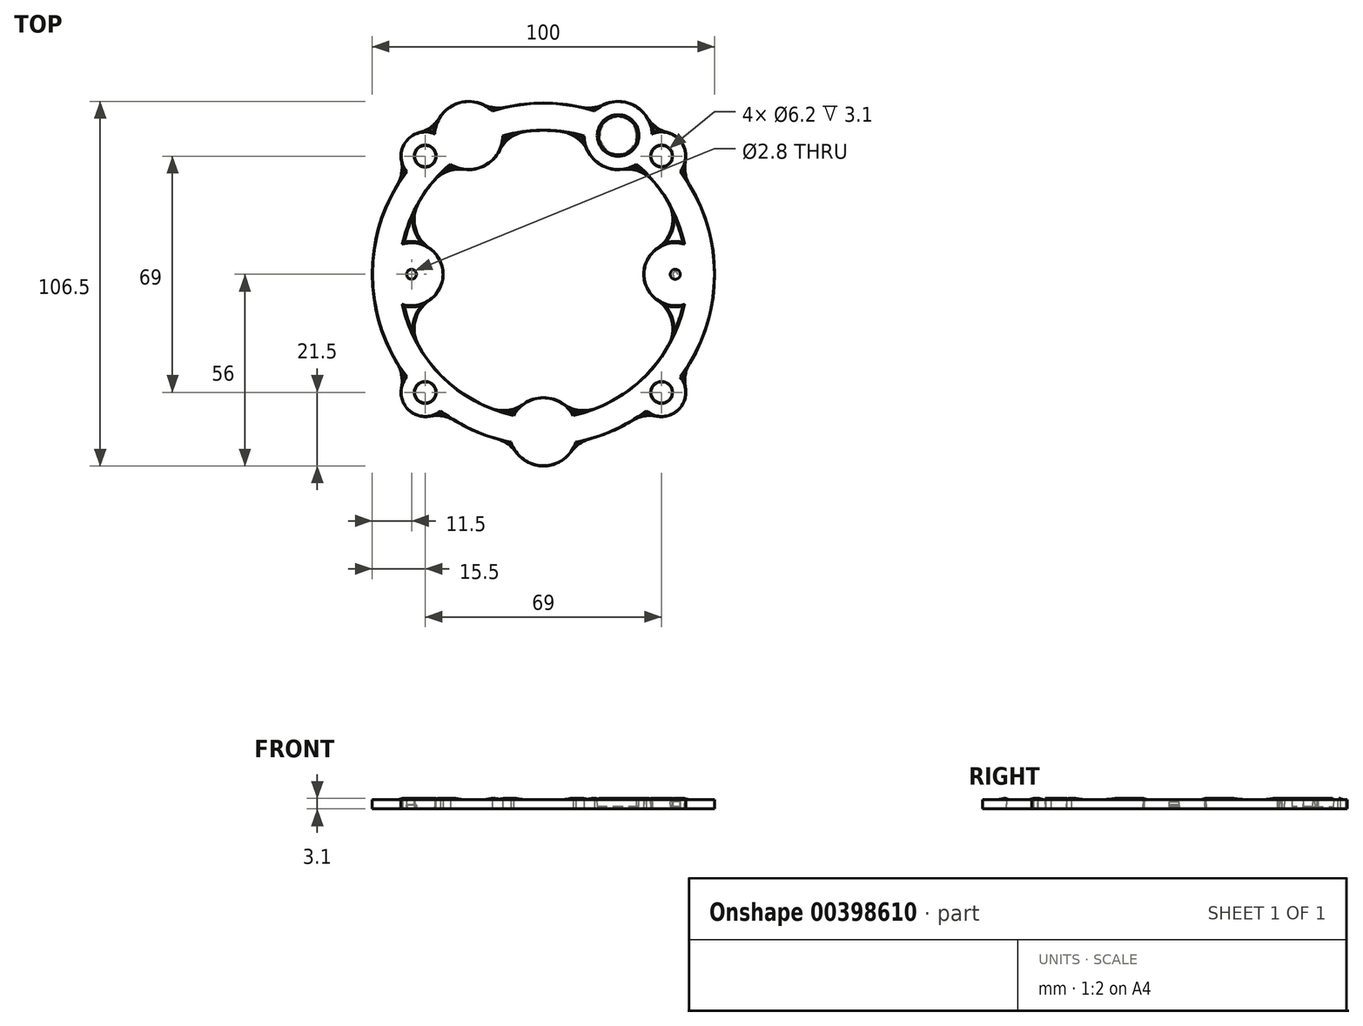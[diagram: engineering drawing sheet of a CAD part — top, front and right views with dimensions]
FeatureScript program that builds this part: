
annotation { "Feature Type Name" : "Feature", "Feature Type Description" : "" }
export const myFeature = defineFeature(function(context is Context, id is Id, definition is map)
    precondition{}
    {
        {
            var Q0;
            Q0=qCreatedBy(makeId("Top.planeOp"),FACE);
            var sketch = newSketch(context, id + "F0", { "sketchPlane" : qUnion([Q0])});
            skCircle(sketch, "E0", {"center": v(0, 0) * mm, "radius": 56 * mm, "construction": true});
            skCircle(sketch, "E1", {"center": v(0, 0) * mm, "radius": 38.5 * mm, "construction": true});
            skLineSegment(sketch, "E2.bottom", {"start": v(-34.5, 34.5) * mm, "end": v(34.5, 34.5) * mm, "construction": true});
            skLineSegment(sketch, "E2.top", {"start": v(-34.5, -34.5) * mm, "end": v(34.5, -34.5) * mm, "construction": true});
            skLineSegment(sketch, "E2.left", {"start": v(-34.5, 34.5) * mm, "end": v(-34.5, -34.5) * mm, "construction": true});
            skLineSegment(sketch, "E2.right", {"start": v(34.5, 34.5) * mm, "end": v(34.5, -34.5) * mm, "construction": true});
            skCircle(sketch, "E3", {"center": v(-34.5, 34.5) * mm, "radius": 3.1 * mm});
            skCircle(sketch, "E4.1.0", {"center": v(-34.5, -34.5) * mm, "radius": 3.1 * mm});
            skCircle(sketch, "E4.2.0", {"center": v(34.5, -34.5) * mm, "radius": 3.1 * mm});
            skCircle(sketch, "E4.3.0", {"center": v(34.5, 34.5) * mm, "radius": 3.1 * mm});
            skCircle(sketch, "E5", {"center": v(-38.5, 0) * mm, "radius": 1.4 * mm});
            skPoint(sketch, "E5.centerSnap0", {"position": v(-34.5, 0) * mm});
            skCircle(sketch, "E6.MirrorC", {"center": v(38.5, 0) * mm, "radius": 1.4 * mm});
            skCircle(sketch, "E7", {"center": v(-21.81, 40.5) * mm, "radius": 6 * mm});
            skCircle(sketch, "E8.MirrorC", {"center": v(21.81, 40.5) * mm, "radius": 6 * mm});
            skLineSegment(sketch, "E9.bottom", {"start": v(-24.25, 29.25) * mm, "end": v(24.25, 29.25) * mm});
            skLineSegment(sketch, "E9.top", {"start": v(-24.25, -29.25) * mm, "end": v(24.25, -29.25) * mm});
            skLineSegment(sketch, "E9.left", {"start": v(-29.25, 24.25) * mm, "end": v(-29.25, -24.25) * mm});
            skLineSegment(sketch, "E9.right", {"start": v(29.25, 24.25) * mm, "end": v(29.25, -24.25) * mm});
            skPoint(sketch, "E10.visualSharp", {"position": v(-29.25, 29.25) * mm});
            skArc(sketch, "E10.filletArc", {"start": v(-24.25, 29.25) * mm, "mid": v(-27.79, 27.79) * mm, "end": v(-29.25, 24.25) * mm});
            skPoint(sketch, "E11.visualSharp", {"position": v(29.25, 29.25) * mm});
            skArc(sketch, "E11.filletArc", {"start": v(29.25, 24.25) * mm, "mid": v(27.79, 27.79) * mm, "end": v(24.25, 29.25) * mm});
            skPoint(sketch, "E12.visualSharp", {"position": v(29.25, -29.25) * mm});
            skArc(sketch, "E12.filletArc", {"start": v(24.25, -29.25) * mm, "mid": v(27.79, -27.79) * mm, "end": v(29.25, -24.25) * mm});
            skPoint(sketch, "E13.visualSharp", {"position": v(-29.25, -29.25) * mm});
            skArc(sketch, "E13.filletArc", {"start": v(-29.25, -24.25) * mm, "mid": v(-27.79, -27.79) * mm, "end": v(-24.25, -29.25) * mm});
            skCircle(sketch, "E14", {"center": v(0, -46) * mm, "radius": 6 * mm});
            skPoint(sketch, "E14.centerSnap0", {"position": v(0, -29.25) * mm});
            skArc(sketch, "E15.0", {"start": v(-14.9, 47.73) * mm, "mid": v(-25.48, 49.8) * mm, "end": v(-31.8, 41.06) * mm});
            skArc(sketch, "E16.MirrorC", {"start": v(14.9, 47.73) * mm, "mid": v(26.55, 49.3) * mm, "end": v(31.65, 38.7) * mm});
            skArc(sketch, "E17", {"start": v(8.7, -41.09) * mm, "mid": v(0, -36) * mm, "end": v(-8.7, -41.09) * mm});
            skArc(sketch, "E18.0", {"start": v(-27.71, 32.42) * mm, "mid": v(-27.48, 33.45) * mm, "end": v(-27.4, 34.5) * mm});
            skArc(sketch, "E19.1.0", {"start": v(-34.5, -27.4) * mm, "mid": v(-39.52, -39.52) * mm, "end": v(-27.4, -34.5) * mm});
            skArc(sketch, "E19.2.0", {"start": v(27.4, -34.5) * mm, "mid": v(39.52, -39.52) * mm, "end": v(34.5, -27.4) * mm});
            skArc(sketch, "E19.3.0", {"start": v(27.75, 36.69) * mm, "mid": v(27.4, 34.56) * mm, "end": v(27.71, 32.42) * mm});
            skArc(sketch, "E20", {"start": v(-41.05, -8.9) * mm, "mid": v(-29.25, 0) * mm, "end": v(-41.05, 8.9) * mm});
            skArc(sketch, "E21.MirrorC", {"start": v(41.05, -8.9) * mm, "mid": v(29.25, 0) * mm, "end": v(41.05, 8.9) * mm});
            skCircle(sketch, "E22", {"center": v(0, 0) * mm, "radius": 46 * mm, "construction": true});
            skArc(sketch, "E23.0", {"start": v(-30, -40) * mm, "mid": v(-20.27, -45.7) * mm, "end": v(-9.51, -49.09) * mm});
            skArc(sketch, "E24.0", {"start": v(8.7, -41.09) * mm, "mid": v(29.63, -29.76) * mm, "end": v(41.05, -8.9) * mm});
            skArc(sketch, "E25.trimOffspring", {"start": v(40, -30) * mm, "mid": v(50, 0) * mm, "end": v(40, 30) * mm});
            skArc(sketch, "E26.trimOffspring", {"start": v(9.51, -49.09) * mm, "mid": v(20.27, -45.7) * mm, "end": v(30, -40) * mm});
            skArc(sketch, "E27.trimOffspring", {"start": v(-41.05, -8.9) * mm, "mid": v(-29.63, -29.76) * mm, "end": v(-8.7, -41.09) * mm});
            skArc(sketch, "E28.trimOffspring", {"start": v(41.05, 8.9) * mm, "mid": v(36.01, 21.62) * mm, "end": v(27.15, 32.04) * mm});
            skArc(sketch, "E29.trimOffspring", {"start": v(-40, 30) * mm, "mid": v(-50, 0) * mm, "end": v(-40, -30) * mm});
            skArc(sketch, "E30.trimOffspring", {"start": v(-23.57, 34.76) * mm, "mid": v(-23.76, 34.63) * mm, "end": v(-23.95, 34.5) * mm});
            skArc(sketch, "E31.trimOffspring", {"start": v(-27.15, 32.04) * mm, "mid": v(-36.01, 21.62) * mm, "end": v(-41.05, 8.9) * mm});
            skArc(sketch, "E32.trimOffspring", {"start": v(-31.8, 41.06) * mm, "mid": v(-40.2, 38.73) * mm, "end": v(-40, 30) * mm});
            skArc(sketch, "E33.trimOffspring", {"start": v(-30.05, 34.83) * mm, "mid": v(-29.93, 34.66) * mm, "end": v(-29.81, 34.5) * mm});
            skArc(sketch, "E34.trimOffspring", {"start": v(-27.15, 32.04) * mm, "mid": v(-17.07, 31.7) * mm, "end": v(-11.81, 40.3) * mm});
            skArc(sketch, "E35.trimOffspring", {"start": v(11.81, 40.3) * mm, "mid": v(0, 42) * mm, "end": v(-11.81, 40.3) * mm});
            skArc(sketch, "E36.trimOffspring", {"start": v(23.95, 34.5) * mm, "mid": v(23.76, 34.63) * mm, "end": v(23.57, 34.76) * mm});
            skArc(sketch, "E37.trimOffspring", {"start": v(30.05, 34.83) * mm, "mid": v(28.98, 33.53) * mm, "end": v(27.71, 32.42) * mm});
            skArc(sketch, "E38.trimOffspring", {"start": v(31.65, 38.7) * mm, "mid": v(30.83, 39.36) * mm, "end": v(30, 40) * mm});
            skArc(sketch, "E39.trimOffspring", {"start": v(14.9, 47.73) * mm, "mid": v(0, 50) * mm, "end": v(-14.9, 47.73) * mm});
            skArc(sketch, "E40.trimOffspring", {"start": v(27.15, 32.04) * mm, "mid": v(15.4, 32.83) * mm, "end": v(12.54, 44.26) * mm});
            skArc(sketch, "E41.trimOffspring", {"start": v(40, 30) * mm, "mid": v(40.2, 38.73) * mm, "end": v(31.8, 41.06) * mm});
            skArc(sketch, "E42.trimOffspring", {"start": v(34.5, 27.4) * mm, "mid": v(35.6, 27.49) * mm, "end": v(36.69, 27.75) * mm});
            skArc(sketch, "E43.trimOffspring", {"start": v(-9.94, -44.91) * mm, "mid": v(0, -56) * mm, "end": v(9.94, -44.91) * mm});
            skSolve(sketch);
        }
        {
            var Q0;
            {var subQ0=sQuery(id+"F0.wireOp",EDGE,"E23.0");var subQ1=sQuery(id+"F0.wireOp",EDGE,"E4.1.0");var subQ2=makeQuery(id+"F0.imprint","INTERSECT",VERTEX,{"disambiguationData":[OD(0.0)],"derivedFrom":[subQ1,subQ0]});Q0=makeQuery(id+"F0.imprint","IMPRINT",FACE,{"disambiguationData":[TD([[makeQuery(id+"F0.imprint","IMPRINT",EDGE,{"disambiguationData":[TD([[subQ2,-1.0]])],"derivedFrom":subQ1}),-1.0]])]});}
            var Q1;
            {var subQ0=sQuery(id+"F0.wireOp",EDGE,"E23.0");var subQ1=sQuery(id+"F0.wireOp",EDGE,"E4.2.0");var subQ2=makeQuery(id+"F0.imprint","INTERSECT",VERTEX,{"disambiguationData":[OD(0.0)],"derivedFrom":[subQ1,subQ0]});Q1=makeQuery(id+"F0.imprint","IMPRINT",FACE,{"disambiguationData":[TD([[makeQuery(id+"F0.imprint","IMPRINT",EDGE,{"disambiguationData":[TD([[subQ2,-1.0]])],"derivedFrom":subQ1}),-1.0]])]});}
            var Q2;
            {var subQ3=sQuery(id+"F0.wireOp",EDGE,"E23.0");var subQ5=sQuery(id+"F0.wireOp",EDGE,"E3");var subQ6=makeQuery(id+"F0.imprint","INTERSECT",VERTEX,{"disambiguationData":[OD(0.0)],"derivedFrom":[subQ5,subQ3]});Q2=makeQuery(id+"F0.imprint","IMPRINT",FACE,{"disambiguationData":[TD([[makeQuery(id+"F0.imprint","IMPRINT",EDGE,{"disambiguationData":[TD([[subQ6,-1.0]])],"derivedFrom":subQ5}),-1.0]])]});}
            var Q3;
            {var subQ0=sQuery(id+"F0.wireOp",EDGE,"E23.0");var subQ1=sQuery(id+"F0.wireOp",EDGE,"E4.1.0");var subQ2=makeQuery(id+"F0.imprint","INTERSECT",VERTEX,{"disambiguationData":[OD(0.0)],"derivedFrom":[subQ1,subQ0]});Q3=makeQuery(id+"F0.imprint","IMPRINT",FACE,{"disambiguationData":[TD([[makeQuery(id+"F0.imprint","IMPRINT",EDGE,{"disambiguationData":[TD([[subQ2,1.0]])],"derivedFrom":subQ1}),-1.0]])]});}
            var Q4;
            {var subQ0=sQuery(id+"F0.wireOp",EDGE,"E23.0");var subQ1=sQuery(id+"F0.wireOp",EDGE,"E4.2.0");var subQ2=makeQuery(id+"F0.imprint","INTERSECT",VERTEX,{"disambiguationData":[OD(0.0)],"derivedFrom":[subQ1,subQ0]});Q4=makeQuery(id+"F0.imprint","IMPRINT",FACE,{"disambiguationData":[TD([[makeQuery(id+"F0.imprint","IMPRINT",EDGE,{"disambiguationData":[TD([[subQ2,1.0]])],"derivedFrom":subQ1}),-1.0]])]});}
            var Q5;
            {var subQ3=sQuery(id+"F0.wireOp",EDGE,"E23.0");var subQ5=sQuery(id+"F0.wireOp",EDGE,"E4.3.0");var subQ6=makeQuery(id+"F0.imprint","INTERSECT",VERTEX,{"disambiguationData":[OD(0.0)],"derivedFrom":[subQ5,subQ3]});Q5=makeQuery(id+"F0.imprint","IMPRINT",FACE,{"disambiguationData":[TD([[makeQuery(id+"F0.imprint","IMPRINT",EDGE,{"disambiguationData":[TD([[subQ6,-1.0]])],"derivedFrom":subQ5}),-1.0]])]});}
            var Q6;
            {var subQ0=sQuery(id+"F0.wireOp",EDGE,"E23.0");var subQ1=sQuery(id+"F0.wireOp",EDGE,"E14");var subQ2=makeQuery(id+"F0.imprint","INTERSECT",VERTEX,{"disambiguationData":[OD(0.0)],"derivedFrom":[subQ1,subQ0]});Q6=makeQuery(id+"F0.imprint","IMPRINT",FACE,{"disambiguationData":[TD([[makeQuery(id+"F0.imprint","IMPRINT",EDGE,{"disambiguationData":[TD([[subQ2,-1.0]])],"derivedFrom":subQ1}),-1.0]])]});}
            var Q7;
            {var subQ0=sQuery(id+"F0.wireOp",EDGE,"E18.0");var subQ1=sQuery(id+"F0.wireOp",EDGE,"E15.0");var subQ2=makeQuery(id+"F0.imprint","INTERSECT",VERTEX,{"disambiguationData":[OD(0.0)],"derivedFrom":[subQ1,subQ0]});Q7=makeQuery(id+"F0.imprint","IMPRINT",FACE,{"disambiguationData":[TD([[makeQuery(id+"F0.imprint","IMPRINT",EDGE,{"disambiguationData":[TD([[subQ2,-1.0]])],"derivedFrom":subQ1}),1.0]])]});}
            var Q8;
            {var subQ0=sQuery(id+"F0.wireOp",EDGE,"E23.0");var subQ1=sQuery(id+"F0.wireOp",EDGE,"E15.0");var subQ2=makeQuery(id+"F0.imprint","INTERSECT",VERTEX,{"disambiguationData":[OD(0.0)],"derivedFrom":[subQ1,subQ0]});Q8=makeQuery(id+"F0.imprint","IMPRINT",FACE,{"disambiguationData":[TD([[makeQuery(id+"F0.imprint","IMPRINT",EDGE,{"disambiguationData":[TD([[subQ2,1.0]])],"derivedFrom":subQ1}),-1.0]])]});}
            var Q9;
            {var subQ0=sQuery(id+"F0.wireOp",EDGE,"E19.3.0");var subQ1=sQuery(id+"F0.wireOp",EDGE,"E16.MirrorC");var subQ2=makeQuery(id+"F0.imprint","INTERSECT",VERTEX,{"disambiguationData":[OD(0.0)],"derivedFrom":[subQ1,subQ0]});Q9=makeQuery(id+"F0.imprint","IMPRINT",FACE,{"disambiguationData":[TD([[makeQuery(id+"F0.imprint","IMPRINT",EDGE,{"disambiguationData":[TD([[subQ2,-1.0]])],"derivedFrom":subQ1}),-1.0]])]});}
            var Q10;
            {var subQ0=sQuery(id+"F0.wireOp",EDGE,"E23.0");var subQ1=sQuery(id+"F0.wireOp",EDGE,"E3");var subQ2=makeQuery(id+"F0.imprint","INTERSECT",VERTEX,{"disambiguationData":[OD(0.0)],"derivedFrom":[subQ1,subQ0]});Q10=makeQuery(id+"F0.imprint","IMPRINT",FACE,{"disambiguationData":[TD([[makeQuery(id+"F0.imprint","IMPRINT",EDGE,{"disambiguationData":[TD([[subQ2,1.0]])],"derivedFrom":subQ1}),-1.0]])]});}
            var Q11;
            {var subQ0=sQuery(id+"F0.wireOp",EDGE,"E23.0");var subQ3=sQuery(id+"F0.wireOp",EDGE,"E4.3.0");var subQ4=makeQuery(id+"F0.imprint","INTERSECT",VERTEX,{"disambiguationData":[OD(0.0)],"derivedFrom":[subQ3,subQ0]});Q11=makeQuery(id+"F0.imprint","IMPRINT",FACE,{"disambiguationData":[TD([[makeQuery(id+"F0.imprint","IMPRINT",EDGE,{"disambiguationData":[TD([[subQ4,1.0]])],"derivedFrom":subQ3}),-1.0]])]});}
            var Q12;
            {var subQ0=sQuery(id+"F0.wireOp",EDGE,"E23.0");var subQ3=sQuery(id+"F0.wireOp",EDGE,"E7");var subQ8=makeQuery(id+"F0.imprint","INTERSECT",VERTEX,{"disambiguationData":[OD(0.0)],"derivedFrom":[subQ3,subQ0]});Q12=makeQuery(id+"F0.imprint","IMPRINT",FACE,{"disambiguationData":[TD([[makeQuery(id+"F0.imprint","IMPRINT",EDGE,{"disambiguationData":[TD([[subQ8,1.0]])],"derivedFrom":subQ3}),-1.0]])]});}
            var Q13;
            {var subQ0=sQuery(id+"F0.wireOp",EDGE,"E23.0");var subQ1=sQuery(id+"F0.wireOp",EDGE,"E7");var subQ2=makeQuery(id+"F0.imprint","INTERSECT",VERTEX,{"disambiguationData":[OD(1.0)],"derivedFrom":[subQ1,subQ0]});Q13=makeQuery(id+"F0.imprint","IMPRINT",FACE,{"disambiguationData":[TD([[makeQuery(id+"F0.imprint","IMPRINT",EDGE,{"disambiguationData":[TD([[subQ2,1.0]])],"derivedFrom":subQ1}),-1.0]])]});}
            var Q14;
            {var subQ0=sQuery(id+"F0.wireOp",EDGE,"E23.0");var subQ1=sQuery(id+"F0.wireOp",EDGE,"E8.MirrorC");var subQ2=makeQuery(id+"F0.imprint","INTERSECT",VERTEX,{"disambiguationData":[OD(1.0)],"derivedFrom":[subQ1,subQ0]});Q14=makeQuery(id+"F0.imprint","IMPRINT",FACE,{"disambiguationData":[TD([[makeQuery(id+"F0.imprint","IMPRINT",EDGE,{"disambiguationData":[TD([[subQ2,1.0]])],"derivedFrom":subQ1}),1.0]])]});}
            var Q15;
            {var subQ0=sQuery(id+"F0.wireOp",EDGE,"E24.0");var subQ1=sQuery(id+"F0.wireOp",EDGE,"E14");var subQ2=makeQuery(id+"F0.imprint","INTERSECT",VERTEX,{"disambiguationData":[OD(0.0)],"derivedFrom":[subQ1,subQ0]});Q15=makeQuery(id+"F0.imprint","IMPRINT",FACE,{"disambiguationData":[TD([[makeQuery(id+"F0.imprint","IMPRINT",EDGE,{"disambiguationData":[TD([[subQ2,-1.0]])],"derivedFrom":subQ1}),-1.0]])]});}
            var Q16;
            {var subQ0=sQuery(id+"F0.wireOp",EDGE,"E24.0");var subQ1=sQuery(id+"F0.wireOp",EDGE,"E14");var subQ2=makeQuery(id+"F0.imprint","INTERSECT",VERTEX,{"disambiguationData":[OD(1.0)],"derivedFrom":[subQ1,subQ0]});Q16=makeQuery(id+"F0.imprint","IMPRINT",FACE,{"disambiguationData":[TD([[makeQuery(id+"F0.imprint","IMPRINT",EDGE,{"disambiguationData":[TD([[subQ2,1.0]])],"derivedFrom":subQ1}),-1.0]])]});}
            var Q17;
            {var subQ4=sQuery(id+"F0.wireOp",EDGE,"E18.0");var subQ6=sQuery(id+"F0.wireOp",EDGE,"E15.0");var subQ7=makeQuery(id+"F0.imprint","INTERSECT",VERTEX,{"disambiguationData":[OD(1.0)],"derivedFrom":[subQ6,subQ4]});Q17=makeQuery(id+"F0.imprint","IMPRINT",FACE,{"disambiguationData":[TD([[makeQuery(id+"F0.imprint","IMPRINT",EDGE,{"disambiguationData":[TD([[subQ7,-1.0]])],"derivedFrom":subQ6}),-1.0]])]});}
            var Q18;
            {var subQ1=sQuery(id+"F0.wireOp",EDGE,"E19.3.0");var subQ3=sQuery(id+"F0.wireOp",EDGE,"E16.MirrorC");var subQ4=makeQuery(id+"F0.imprint","INTERSECT",VERTEX,{"disambiguationData":[OD(1.0)],"derivedFrom":[subQ3,subQ1]});Q18=makeQuery(id+"F0.imprint","IMPRINT",FACE,{"disambiguationData":[TD([[makeQuery(id+"F0.imprint","IMPRINT",EDGE,{"disambiguationData":[TD([[subQ4,-1.0]])],"derivedFrom":subQ3}),1.0]])]});}
            var Q19;
            {var subQ0=sQuery(id+"F0.wireOp",EDGE,"E24.0");var subQ1=sQuery(id+"F0.wireOp",EDGE,"E7");var subQ2=makeQuery(id+"F0.imprint","INTERSECT",VERTEX,{"disambiguationData":[OD(0.0)],"derivedFrom":[subQ1,subQ0]});Q19=makeQuery(id+"F0.imprint","IMPRINT",FACE,{"disambiguationData":[TD([[makeQuery(id+"F0.imprint","IMPRINT",EDGE,{"disambiguationData":[TD([[subQ2,-1.0]])],"derivedFrom":subQ1}),-1.0]])]});}
            var Q20;
            {var subQ5=sQuery(id+"F0.wireOp",EDGE,"E7");var subQ7=sQuery(id+"F0.wireOp",EDGE,"E23.0");var subQ8=makeQuery(id+"F0.imprint","INTERSECT",VERTEX,{"disambiguationData":[OD(0.0)],"derivedFrom":[subQ5,subQ7]});Q20=makeQuery(id+"F0.imprint","IMPRINT",FACE,{"disambiguationData":[TD([[makeQuery(id+"F0.imprint","IMPRINT",EDGE,{"disambiguationData":[TD([[subQ8,-1.0]])],"derivedFrom":subQ5}),-1.0]])]});}
            var Q21;
            {var subQ0=sQuery(id+"F0.wireOp",EDGE,"E24.0");var subQ1=sQuery(id+"F0.wireOp",EDGE,"E8.MirrorC");var subQ2=makeQuery(id+"F0.imprint","INTERSECT",VERTEX,{"disambiguationData":[OD(0.0)],"derivedFrom":[subQ1,subQ0]});Q21=makeQuery(id+"F0.imprint","IMPRINT",FACE,{"disambiguationData":[TD([[makeQuery(id+"F0.imprint","IMPRINT",EDGE,{"disambiguationData":[TD([[subQ2,-1.0]])],"derivedFrom":subQ1}),1.0]])]});}
            var Q22;
            {var subQ0=sQuery(id+"F0.wireOp",EDGE,"E24.0");var subQ1=sQuery(id+"F0.wireOp",EDGE,"E8.MirrorC");var subQ2=makeQuery(id+"F0.imprint","INTERSECT",VERTEX,{"disambiguationData":[OD(0.0)],"derivedFrom":[subQ1,subQ0]});Q22=makeQuery(id+"F0.imprint","IMPRINT",FACE,{"disambiguationData":[TD([[makeQuery(id+"F0.imprint","IMPRINT",EDGE,{"disambiguationData":[TD([[subQ2,-1.0]])],"derivedFrom":subQ1}),-1.0]])]});}
            var Q23;
            {var subQ0=sQuery(id+"F0.wireOp",EDGE,"E23.0");var subQ1=sQuery(id+"F0.wireOp",EDGE,"E8.MirrorC");var subQ2=makeQuery(id+"F0.imprint","INTERSECT",VERTEX,{"disambiguationData":[OD(0.0)],"derivedFrom":[subQ1,subQ0]});Q23=makeQuery(id+"F0.imprint","IMPRINT",FACE,{"disambiguationData":[TD([[makeQuery(id+"F0.imprint","IMPRINT",EDGE,{"disambiguationData":[TD([[subQ2,-1.0]])],"derivedFrom":subQ1}),-1.0]])]});}
            var Q24;
            {var subQ0=sQuery(id+"F0.wireOp",EDGE,"E23.0");var subQ1=sQuery(id+"F0.wireOp",EDGE,"E8.MirrorC");var subQ2=makeQuery(id+"F0.imprint","INTERSECT",VERTEX,{"disambiguationData":[OD(0.0)],"derivedFrom":[subQ1,subQ0]});Q24=makeQuery(id+"F0.imprint","IMPRINT",FACE,{"disambiguationData":[TD([[makeQuery(id+"F0.imprint","IMPRINT",EDGE,{"disambiguationData":[TD([[subQ2,1.0]])],"derivedFrom":subQ1}),1.0]])]});}
            var Q25;
            {var subQ3=sQuery(id+"F0.wireOp",EDGE,"E23.0");var subQ7=sQuery(id+"F0.wireOp",EDGE,"E8.MirrorC");var subQ8=makeQuery(id+"F0.imprint","INTERSECT",VERTEX,{"disambiguationData":[OD(0.0)],"derivedFrom":[subQ7,subQ3]});Q25=makeQuery(id+"F0.imprint","IMPRINT",FACE,{"disambiguationData":[TD([[makeQuery(id+"F0.imprint","IMPRINT",EDGE,{"disambiguationData":[TD([[subQ8,-1.0]])],"derivedFrom":subQ7}),1.0]])]});}
            var Q26;
            {var subQ0=sQuery(id+"F0.wireOp",EDGE,"E23.0");var subQ1=sQuery(id+"F0.wireOp",EDGE,"E16.MirrorC");var subQ2=makeQuery(id+"F0.imprint","INTERSECT",VERTEX,{"disambiguationData":[OD(1.0)],"derivedFrom":[subQ1,subQ0]});Q26=makeQuery(id+"F0.imprint","IMPRINT",FACE,{"disambiguationData":[TD([[makeQuery(id+"F0.imprint","IMPRINT",EDGE,{"disambiguationData":[TD([[subQ2,-1.0]])],"derivedFrom":subQ1}),-1.0]])]});}
            var Q27;
            {var subQ0=sQuery(id+"F0.wireOp",EDGE,"E24.0");var subQ1=sQuery(id+"F0.wireOp",EDGE,"E7");var subQ2=makeQuery(id+"F0.imprint","INTERSECT",VERTEX,{"disambiguationData":[OD(0.0)],"derivedFrom":[subQ1,subQ0]});Q27=makeQuery(id+"F0.imprint","IMPRINT",FACE,{"disambiguationData":[TD([[makeQuery(id+"F0.imprint","IMPRINT",EDGE,{"disambiguationData":[TD([[subQ2,-1.0]])],"derivedFrom":subQ1}),1.0]])]});}
            var Q28;
            Q28=makeQuery(id+"F0.imprint","IMPRINT",FACE,{"disambiguationData":[TD([[makeQuery(id+"F0.imprint","IMPRINT",EDGE,{"derivedFrom":sQuery(id+"F0.wireOp",EDGE,"E6.MirrorC")}),1.0]])]});
            var Q29;
            {var subQ0=sQuery(id+"F0.wireOp",EDGE,"E24.0");var subQ1=sQuery(id+"F0.wireOp",EDGE,"E14");var subQ2=makeQuery(id+"F0.imprint","INTERSECT",VERTEX,{"disambiguationData":[OD(0.0)],"derivedFrom":[subQ1,subQ0]});Q29=makeQuery(id+"F0.imprint","IMPRINT",FACE,{"disambiguationData":[TD([[makeQuery(id+"F0.imprint","IMPRINT",EDGE,{"disambiguationData":[TD([[subQ2,1.0]])],"derivedFrom":subQ1}),1.0]])]});}
            var Q30;
            {var subQ0=sQuery(id+"F0.wireOp",EDGE,"E23.0");var subQ1=sQuery(id+"F0.wireOp",EDGE,"E7");var subQ2=makeQuery(id+"F0.imprint","INTERSECT",VERTEX,{"disambiguationData":[OD(0.0)],"derivedFrom":[subQ1,subQ0]});Q30=makeQuery(id+"F0.imprint","IMPRINT",FACE,{"disambiguationData":[TD([[makeQuery(id+"F0.imprint","IMPRINT",EDGE,{"disambiguationData":[TD([[subQ2,-1.0]])],"derivedFrom":subQ1}),1.0]])]});}
            var Q31;
            {var subQ0=sQuery(id+"F0.wireOp",EDGE,"E24.0");var subQ1=sQuery(id+"F0.wireOp",EDGE,"E14");var subQ2=makeQuery(id+"F0.imprint","INTERSECT",VERTEX,{"disambiguationData":[OD(0.0)],"derivedFrom":[subQ1,subQ0]});Q31=makeQuery(id+"F0.imprint","IMPRINT",FACE,{"disambiguationData":[TD([[makeQuery(id+"F0.imprint","IMPRINT",EDGE,{"disambiguationData":[TD([[subQ2,-1.0]])],"derivedFrom":subQ1}),1.0]])]});}
            var Q32;
            {var subQ0=sQuery(id+"F0.wireOp",EDGE,"E24.0");var subQ1=sQuery(id+"F0.wireOp",EDGE,"E20");var subQ2=makeQuery(id+"F0.imprint","INTERSECT",VERTEX,{"disambiguationData":[OD(0.0)],"derivedFrom":[subQ1,subQ0]});Q32=makeQuery(id+"F0.imprint","IMPRINT",FACE,{"disambiguationData":[TD([[makeQuery(id+"F0.imprint","IMPRINT",EDGE,{"disambiguationData":[TD([[subQ2,-1.0]])],"derivedFrom":subQ1}),1.0]])]});}
            var Q33;
            Q33=makeQuery(id+"F0.imprint","IMPRINT",FACE,{"disambiguationData":[TD([[makeQuery(id+"F0.imprint","IMPRINT",EDGE,{"derivedFrom":sQuery(id+"F0.wireOp",EDGE,"E5")}),-1.0]])]});
            var Q34;
            {var subQ0=sQuery(id+"F0.wireOp",EDGE,"E24.0");var subQ1=sQuery(id+"F0.wireOp",EDGE,"E14");var subQ2=makeQuery(id+"F0.imprint","INTERSECT",VERTEX,{"disambiguationData":[OD(0.0)],"derivedFrom":[subQ1,subQ0]});Q34=makeQuery(id+"F0.imprint","IMPRINT",FACE,{"disambiguationData":[TD([[makeQuery(id+"F0.imprint","IMPRINT",EDGE,{"disambiguationData":[TD([[subQ2,1.0]])],"derivedFrom":subQ1}),-1.0]])]});}
            var Q35;
            {var subQ0=sQuery(id+"F0.wireOp",EDGE,"E23.0");var subQ1=sQuery(id+"F0.wireOp",EDGE,"E8.MirrorC");var subQ2=makeQuery(id+"F0.imprint","INTERSECT",VERTEX,{"disambiguationData":[OD(0.0)],"derivedFrom":[subQ1,subQ0]});Q35=makeQuery(id+"F0.imprint","IMPRINT",FACE,{"disambiguationData":[TD([[makeQuery(id+"F0.imprint","IMPRINT",EDGE,{"disambiguationData":[TD([[subQ2,1.0]])],"derivedFrom":subQ1}),-1.0]])]});}
            var Q36;
            {var subQ0=sQuery(id+"F0.wireOp",EDGE,"E24.0");var subQ1=sQuery(id+"F0.wireOp",EDGE,"E21.MirrorC");var subQ2=makeQuery(id+"F0.imprint","INTERSECT",VERTEX,{"disambiguationData":[OD(0.0)],"derivedFrom":[subQ1,subQ0]});Q36=makeQuery(id+"F0.imprint","IMPRINT",FACE,{"disambiguationData":[TD([[makeQuery(id+"F0.imprint","IMPRINT",EDGE,{"disambiguationData":[TD([[subQ2,-1.0]])],"derivedFrom":subQ1}),-1.0]])]});}
            var Q37;
            {var subQ0=sQuery(id+"F0.wireOp",EDGE,"E23.0");var subQ1=sQuery(id+"F0.wireOp",EDGE,"E15.0");var subQ2=makeQuery(id+"F0.imprint","INTERSECT",VERTEX,{"disambiguationData":[OD(1.0)],"derivedFrom":[subQ1,subQ0]});Q37=makeQuery(id+"F0.imprint","IMPRINT",FACE,{"disambiguationData":[TD([[makeQuery(id+"F0.imprint","IMPRINT",EDGE,{"disambiguationData":[TD([[subQ2,-1.0]])],"derivedFrom":subQ1}),1.0]])]});}
            var Q38;
            {var subQ0=sQuery(id+"F0.wireOp",EDGE,"E23.0");var subQ1=sQuery(id+"F0.wireOp",EDGE,"E4.1.0");var subQ2=makeQuery(id+"F0.imprint","INTERSECT",VERTEX,{"disambiguationData":[OD(0.0)],"derivedFrom":[subQ1,subQ0]});Q38=makeQuery(id+"F0.imprint","IMPRINT",FACE,{"disambiguationData":[TD([[makeQuery(id+"F0.imprint","IMPRINT",EDGE,{"disambiguationData":[TD([[subQ2,-1.0]])],"derivedFrom":subQ1}),1.0]])]});}
            var Q39;
            {var subQ0=sQuery(id+"F0.wireOp",EDGE,"E23.0");var subQ1=sQuery(id+"F0.wireOp",EDGE,"E7");var subQ2=makeQuery(id+"F0.imprint","INTERSECT",VERTEX,{"disambiguationData":[OD(0.0)],"derivedFrom":[subQ1,subQ0]});Q39=makeQuery(id+"F0.imprint","IMPRINT",FACE,{"disambiguationData":[TD([[makeQuery(id+"F0.imprint","IMPRINT",EDGE,{"disambiguationData":[TD([[subQ2,1.0]])],"derivedFrom":subQ1}),1.0]])]});}
            var Q40;
            {var subQ0=sQuery(id+"F0.wireOp",EDGE,"E23.0");var subQ1=sQuery(id+"F0.wireOp",EDGE,"E4.3.0");var subQ2=makeQuery(id+"F0.imprint","INTERSECT",VERTEX,{"disambiguationData":[OD(0.0)],"derivedFrom":[subQ1,subQ0]});Q40=makeQuery(id+"F0.imprint","IMPRINT",FACE,{"disambiguationData":[TD([[makeQuery(id+"F0.imprint","IMPRINT",EDGE,{"disambiguationData":[TD([[subQ2,-1.0]])],"derivedFrom":subQ1}),1.0]])]});}
            var Q41;
            {var subQ0=sQuery(id+"F0.wireOp",EDGE,"E23.0");var subQ1=sQuery(id+"F0.wireOp",EDGE,"E3");var subQ2=makeQuery(id+"F0.imprint","INTERSECT",VERTEX,{"disambiguationData":[OD(0.0)],"derivedFrom":[subQ1,subQ0]});Q41=makeQuery(id+"F0.imprint","IMPRINT",FACE,{"disambiguationData":[TD([[makeQuery(id+"F0.imprint","IMPRINT",EDGE,{"disambiguationData":[TD([[subQ2,-1.0]])],"derivedFrom":subQ1}),1.0]])]});}
            var Q42;
            {var subQ0=sQuery(id+"F0.wireOp",EDGE,"E23.0");var subQ1=sQuery(id+"F0.wireOp",EDGE,"E4.2.0");var subQ2=makeQuery(id+"F0.imprint","INTERSECT",VERTEX,{"disambiguationData":[OD(0.0)],"derivedFrom":[subQ1,subQ0]});Q42=makeQuery(id+"F0.imprint","IMPRINT",FACE,{"disambiguationData":[TD([[makeQuery(id+"F0.imprint","IMPRINT",EDGE,{"disambiguationData":[TD([[subQ2,-1.0]])],"derivedFrom":subQ1}),1.0]])]});}
            var Q43;
            {var subQ0=sQuery(id+"F0.wireOp",EDGE,"E23.0");var subQ1=sQuery(id+"F0.wireOp",EDGE,"E14");var subQ2=makeQuery(id+"F0.imprint","INTERSECT",VERTEX,{"disambiguationData":[OD(0.0)],"derivedFrom":[subQ1,subQ0]});Q43=makeQuery(id+"F0.imprint","IMPRINT",FACE,{"disambiguationData":[TD([[makeQuery(id+"F0.imprint","IMPRINT",EDGE,{"disambiguationData":[TD([[subQ2,-1.0]])],"derivedFrom":subQ1}),1.0]])]});}
            extrude(context, id + "F1", {"entities" : qUnion([Q0, Q1, Q2, Q3, Q4, Q5, Q6, Q7, Q8, Q9, Q10, Q11, Q12, Q13, Q14, Q15, Q16, Q17, Q18, Q19, Q20, Q21, Q22, Q23, Q24, Q25, Q26, Q27, Q28, Q29, Q30, Q31, Q32, Q33, Q34, Q35, Q36, Q37, Q38, Q39, Q40, Q41, Q42, Q43]), "depth" : 3.1 * mm});
        }
        {
            var Q0;
            Q0=makeQuery(id+"F1.opExtrude","SWEPT_EDGE",EDGE,{"disambiguationData":[OSD([sQuery(id+"F0.wireOp",EDGE,"E19.1.0"),sQuery(id+"F0.wireOp",EDGE,"E23.0")])]});
            var Q1;
            Q1=makeQuery(id+"F1.opExtrude","SWEPT_EDGE",EDGE,{"disambiguationData":[OSD([sQuery(id+"F0.wireOp",EDGE,"E17"),sQuery(id+"F0.wireOp",EDGE,"E24.0")])]});
            var Q2;
            Q2=makeQuery(id+"F1.opExtrude","SWEPT_EDGE",EDGE,{"disambiguationData":[OSD([sQuery(id+"F0.wireOp",EDGE,"E17"),sQuery(id+"F0.wireOp",EDGE,"E27.trimOffspring")])]});
            var Q3;
            Q3=makeQuery(id+"F1.opExtrude","SWEPT_EDGE",EDGE,{"disambiguationData":[OSD([sQuery(id+"F0.wireOp",EDGE,"E23.0"),sQuery(id+"F0.wireOp",EDGE,"E43.trimOffspring")])]});
            var Q4;
            Q4=makeQuery(id+"F1.opExtrude","SWEPT_EDGE",EDGE,{"disambiguationData":[OSD([sQuery(id+"F0.wireOp",EDGE,"E19.2.0"),sQuery(id+"F0.wireOp",EDGE,"E25.trimOffspring")])]});
            var Q5;
            Q5=makeQuery(id+"F1.opExtrude","SWEPT_EDGE",EDGE,{"disambiguationData":[OSD([sQuery(id+"F0.wireOp",EDGE,"E19.2.0"),sQuery(id+"F0.wireOp",EDGE,"E26.trimOffspring")])]});
            var Q6;
            Q6=makeQuery(id+"F1.opExtrude","SWEPT_EDGE",EDGE,{"disambiguationData":[OSD([sQuery(id+"F0.wireOp",EDGE,"E21.MirrorC"),sQuery(id+"F0.wireOp",EDGE,"E24.0")])]});
            var Q7;
            Q7=makeQuery(id+"F1.opExtrude","SWEPT_EDGE",EDGE,{"disambiguationData":[OSD([sQuery(id+"F0.wireOp",EDGE,"E20"),sQuery(id+"F0.wireOp",EDGE,"E27.trimOffspring")])]});
            var Q8;
            Q8=makeQuery(id+"F1.opExtrude","SWEPT_EDGE",EDGE,{"disambiguationData":[OSD([sQuery(id+"F0.wireOp",EDGE,"E20"),sQuery(id+"F0.wireOp",EDGE,"E31.trimOffspring")])]});
            var Q9;
            Q9=makeQuery(id+"F1.opExtrude","SWEPT_EDGE",EDGE,{"disambiguationData":[OSD([sQuery(id+"F0.wireOp",EDGE,"E15.0"),sQuery(id+"F0.wireOp",EDGE,"E39.trimOffspring")])]});
            var Q10;
            Q10=makeQuery(id+"F1.opExtrude","SWEPT_EDGE",EDGE,{"disambiguationData":[OSD([sQuery(id+"F0.wireOp",EDGE,"E15.0"),sQuery(id+"F0.wireOp",EDGE,"E32.trimOffspring")])]});
            var Q11;
            Q11=makeQuery(id+"F1.opExtrude","SWEPT_EDGE",EDGE,{"disambiguationData":[OSD([sQuery(id+"F0.wireOp",EDGE,"E16.MirrorC"),sQuery(id+"F0.wireOp",EDGE,"E39.trimOffspring")])]});
            var Q12;
            Q12=makeQuery(id+"F1.opExtrude","SWEPT_EDGE",EDGE,{"disambiguationData":[OSD([sQuery(id+"F0.wireOp",EDGE,"E16.MirrorC"),sQuery(id+"F0.wireOp",EDGE,"E41.trimOffspring")])]});
            var Q13;
            Q13=makeQuery(id+"F1.opExtrude","SWEPT_EDGE",EDGE,{"disambiguationData":[OSD([sQuery(id+"F0.wireOp",EDGE,"E31.trimOffspring"),sQuery(id+"F0.wireOp",EDGE,"E34.trimOffspring")])]});
            var Q14;
            Q14=makeQuery(id+"F1.opExtrude","SWEPT_EDGE",EDGE,{"disambiguationData":[OSD([sQuery(id+"F0.wireOp",EDGE,"E34.trimOffspring"),sQuery(id+"F0.wireOp",EDGE,"E35.trimOffspring")])]});
            var Q15;
            Q15=makeQuery(id+"F1.opExtrude","SWEPT_EDGE",EDGE,{"disambiguationData":[OSD([sQuery(id+"F0.wireOp",EDGE,"E35.trimOffspring"),sQuery(id+"F0.wireOp",EDGE,"E40.trimOffspring")])]});
            var Q16;
            Q16=makeQuery(id+"F1.opExtrude","SWEPT_EDGE",EDGE,{"disambiguationData":[OSD([sQuery(id+"F0.wireOp",EDGE,"E28.trimOffspring"),sQuery(id+"F0.wireOp",EDGE,"E40.trimOffspring")])]});
            var Q17;
            Q17=makeQuery(id+"F1.opExtrude","SWEPT_EDGE",EDGE,{"disambiguationData":[OSD([sQuery(id+"F0.wireOp",EDGE,"E25.trimOffspring"),sQuery(id+"F0.wireOp",EDGE,"E41.trimOffspring")])]});
            var Q18;
            Q18=makeQuery(id+"F1.opExtrude","SWEPT_EDGE",EDGE,{"disambiguationData":[OSD([sQuery(id+"F0.wireOp",EDGE,"E21.MirrorC"),sQuery(id+"F0.wireOp",EDGE,"E28.trimOffspring")])]});
            var Q19;
            Q19=makeQuery(id+"F1.opExtrude","SWEPT_EDGE",EDGE,{"disambiguationData":[OSD([sQuery(id+"F0.wireOp",EDGE,"E26.trimOffspring"),sQuery(id+"F0.wireOp",EDGE,"E43.trimOffspring")])]});
            var Q20;
            Q20=makeQuery(id+"F1.opExtrude","SWEPT_EDGE",EDGE,{"disambiguationData":[OSD([sQuery(id+"F0.wireOp",EDGE,"E19.1.0"),sQuery(id+"F0.wireOp",EDGE,"E29.trimOffspring")])]});
            var Q21;
            Q21=makeQuery(id+"F1.opExtrude","SWEPT_EDGE",EDGE,{"disambiguationData":[OSD([sQuery(id+"F0.wireOp",EDGE,"E29.trimOffspring"),sQuery(id+"F0.wireOp",EDGE,"E32.trimOffspring")])]});
            fillet(context, id + "F2", {"entities" : qUnion([Q0, Q1, Q2, Q3, Q4, Q5, Q6, Q7, Q8, Q9, Q10, Q11, Q12, Q13, Q14, Q15, Q16, Q17, Q18, Q19, Q20, Q21]), "radius" : 10 * mm, "tangentPropagation" : true, "allowEdgeOverflow" : false});
        }
        {
            var Q0;
            Q0=makeQuery(id+"F0.imprint","IMPRINT",FACE,{"disambiguationData":[TD([[makeQuery(id+"F0.imprint","IMPRINT",EDGE,{"derivedFrom":sQuery(id+"F0.wireOp",EDGE,"E14")}),1.0]])]});
            var Q1;
            Q1=makeQuery(id+"F0.imprint","IMPRINT",FACE,{"disambiguationData":[TD([[makeQuery(id+"F0.imprint","IMPRINT",EDGE,{"derivedFrom":sQuery(id+"F0.wireOp",EDGE,"E8.MirrorC")}),-1.0]])]});
            var Q2;
            Q2=makeQuery(id+"F0.imprint","IMPRINT",FACE,{"disambiguationData":[TD([[makeQuery(id+"F0.imprint","IMPRINT",EDGE,{"derivedFrom":sQuery(id+"F0.wireOp",EDGE,"E7")}),1.0]])]});
            var Q3;
            Q3=makeQuery(id+"F1.opExtrude","CAP_FACE",FACE,{"disambiguationData":[OSD([sQuery(id+"F0.wireOp",EDGE,"E5"),sQuery(id+"F0.wireOp",EDGE,"E6.MirrorC"),sQuery(id+"F0.wireOp",EDGE,"E15.0"),sQuery(id+"F0.wireOp",EDGE,"E16.MirrorC"),sQuery(id+"F0.wireOp",EDGE,"E17"),sQuery(id+"F0.wireOp",EDGE,"E19.1.0"),sQuery(id+"F0.wireOp",EDGE,"E19.2.0"),sQuery(id+"F0.wireOp",EDGE,"E20"),sQuery(id+"F0.wireOp",EDGE,"E21.MirrorC"),sQuery(id+"F0.wireOp",EDGE,"E23.0"),sQuery(id+"F0.wireOp",EDGE,"E24.0"),sQuery(id+"F0.wireOp",EDGE,"E25.trimOffspring"),sQuery(id+"F0.wireOp",EDGE,"E26.trimOffspring"),sQuery(id+"F0.wireOp",EDGE,"E27.trimOffspring"),sQuery(id+"F0.wireOp",EDGE,"E28.trimOffspring"),sQuery(id+"F0.wireOp",EDGE,"E29.trimOffspring"),sQuery(id+"F0.wireOp",EDGE,"E31.trimOffspring"),sQuery(id+"F0.wireOp",EDGE,"E32.trimOffspring"),sQuery(id+"F0.wireOp",EDGE,"E34.trimOffspring"),sQuery(id+"F0.wireOp",EDGE,"E35.trimOffspring"),sQuery(id+"F0.wireOp",EDGE,"E39.trimOffspring"),sQuery(id+"F0.wireOp",EDGE,"E40.trimOffspring"),sQuery(id+"F0.wireOp",EDGE,"E41.trimOffspring"),sQuery(id+"F0.wireOp",EDGE,"E43.trimOffspring")])],"isStart":false});
            extrude(context, id + "F3", {"entities" : qUnion([Q0, Q1, Q2]), "operationType" : NewBodyOperationType.REMOVE, "endBound" : BoundingType.UP_TO_SURFACE, "endBoundEntityFace" : qUnion([Q3]), "depth" : 3.1 * mm, "hasDraft" : true, "draftAngle" : 2 * degree, "draftPullDirection" : true});
        }
        {
            var Q0;
            Q0=makeQuery(id+"F0.imprint","IMPRINT",FACE,{"disambiguationData":[TD([[makeQuery(id+"F0.imprint","IMPRINT",EDGE,{"derivedFrom":sQuery(id+"F0.wireOp",EDGE,"E4.1.0")}),1.0]])]});
            var Q1;
            Q1=makeQuery(id+"F0.imprint","IMPRINT",FACE,{"disambiguationData":[TD([[makeQuery(id+"F0.imprint","IMPRINT",EDGE,{"derivedFrom":sQuery(id+"F0.wireOp",EDGE,"E4.2.0")}),1.0]])]});
            var Q2;
            Q2=makeQuery(id+"F0.imprint","IMPRINT",FACE,{"disambiguationData":[TD([[makeQuery(id+"F0.imprint","IMPRINT",EDGE,{"derivedFrom":sQuery(id+"F0.wireOp",EDGE,"E4.3.0")}),1.0]])]});
            var Q3;
            Q3=makeQuery(id+"F0.imprint","IMPRINT",FACE,{"disambiguationData":[TD([[makeQuery(id+"F0.imprint","IMPRINT",EDGE,{"derivedFrom":sQuery(id+"F0.wireOp",EDGE,"E3")}),1.0]])]});
            var Q4;
            Q4=makeQuery(id+"F1.opExtrude","CAP_FACE",FACE,{"disambiguationData":[OSD([sQuery(id+"F0.wireOp",EDGE,"E5"),sQuery(id+"F0.wireOp",EDGE,"E6.MirrorC"),sQuery(id+"F0.wireOp",EDGE,"E15.0"),sQuery(id+"F0.wireOp",EDGE,"E16.MirrorC"),sQuery(id+"F0.wireOp",EDGE,"E17"),sQuery(id+"F0.wireOp",EDGE,"E19.1.0"),sQuery(id+"F0.wireOp",EDGE,"E19.2.0"),sQuery(id+"F0.wireOp",EDGE,"E20"),sQuery(id+"F0.wireOp",EDGE,"E21.MirrorC"),sQuery(id+"F0.wireOp",EDGE,"E23.0"),sQuery(id+"F0.wireOp",EDGE,"E24.0"),sQuery(id+"F0.wireOp",EDGE,"E25.trimOffspring"),sQuery(id+"F0.wireOp",EDGE,"E26.trimOffspring"),sQuery(id+"F0.wireOp",EDGE,"E27.trimOffspring"),sQuery(id+"F0.wireOp",EDGE,"E28.trimOffspring"),sQuery(id+"F0.wireOp",EDGE,"E29.trimOffspring"),sQuery(id+"F0.wireOp",EDGE,"E31.trimOffspring"),sQuery(id+"F0.wireOp",EDGE,"E32.trimOffspring"),sQuery(id+"F0.wireOp",EDGE,"E34.trimOffspring"),sQuery(id+"F0.wireOp",EDGE,"E35.trimOffspring"),sQuery(id+"F0.wireOp",EDGE,"E39.trimOffspring"),sQuery(id+"F0.wireOp",EDGE,"E40.trimOffspring"),sQuery(id+"F0.wireOp",EDGE,"E41.trimOffspring"),sQuery(id+"F0.wireOp",EDGE,"E43.trimOffspring")])],"isStart":false});
            extrude(context, id + "F4", {"entities" : qUnion([Q0, Q1, Q2, Q3]), "operationType" : NewBodyOperationType.REMOVE, "endBound" : BoundingType.UP_TO_SURFACE, "endBoundEntityFace" : qUnion([Q4]), "depth" : 3.2 * mm});
        }
        {
            var Q0;
            Q0=makeQuery(id+"F1.opExtrude","CAP_FACE",FACE,{"disambiguationData":[OSD([sQuery(id+"F0.wireOp",EDGE,"E5"),sQuery(id+"F0.wireOp",EDGE,"E6.MirrorC"),sQuery(id+"F0.wireOp",EDGE,"E15.0"),sQuery(id+"F0.wireOp",EDGE,"E16.MirrorC"),sQuery(id+"F0.wireOp",EDGE,"E17"),sQuery(id+"F0.wireOp",EDGE,"E19.1.0"),sQuery(id+"F0.wireOp",EDGE,"E19.2.0"),sQuery(id+"F0.wireOp",EDGE,"E20"),sQuery(id+"F0.wireOp",EDGE,"E21.MirrorC"),sQuery(id+"F0.wireOp",EDGE,"E23.0"),sQuery(id+"F0.wireOp",EDGE,"E24.0"),sQuery(id+"F0.wireOp",EDGE,"E25.trimOffspring"),sQuery(id+"F0.wireOp",EDGE,"E26.trimOffspring"),sQuery(id+"F0.wireOp",EDGE,"E27.trimOffspring"),sQuery(id+"F0.wireOp",EDGE,"E28.trimOffspring"),sQuery(id+"F0.wireOp",EDGE,"E29.trimOffspring"),sQuery(id+"F0.wireOp",EDGE,"E31.trimOffspring"),sQuery(id+"F0.wireOp",EDGE,"E32.trimOffspring"),sQuery(id+"F0.wireOp",EDGE,"E34.trimOffspring"),sQuery(id+"F0.wireOp",EDGE,"E35.trimOffspring"),sQuery(id+"F0.wireOp",EDGE,"E39.trimOffspring"),sQuery(id+"F0.wireOp",EDGE,"E40.trimOffspring"),sQuery(id+"F0.wireOp",EDGE,"E41.trimOffspring"),sQuery(id+"F0.wireOp",EDGE,"E43.trimOffspring")])],"isStart":false});
            var sketch = newSketch(context, id + "F5", { "sketchPlane" : qUnion([Q0])});
            skCircle(sketch, "E44.0", {"center": v(-38.5, 0) * mm, "radius": 3 * mm});
            skCircle(sketch, "E45.0", {"center": v(38.5, 0) * mm, "radius": 3 * mm});
            skSolve(sketch);
        }
        {
            var Q0;
            Q0 = qSketchRegion(id + "F5", true);
            extrude(context, id + "F6", {"entities" : qUnion([Q0]), "operationType" : NewBodyOperationType.REMOVE, "oppositeDirection" : true, "depth" : 1 * mm});
        }
        {
            var Q0;
            Q0=makeQuery(id+"F6.boolean.opBoolean","INTERSECT",EDGE,{"derivedFrom":[makeQuery(id+"F1.opExtrude","SWEPT_FACE",FACE,{"disambiguationData":[OSD([sQuery(id+"F0.wireOp",EDGE,"E5")])]}),makeQuery(id+"F6.opExtrude","CAP_FACE",FACE,{"disambiguationData":[OSD([sQuery(id+"F5.wireOp",EDGE,"E44.0")])],"isStart":false})]});
            var Q1;
            Q1=makeQuery(id+"F6.boolean.opBoolean","INTERSECT",EDGE,{"derivedFrom":[makeQuery(id+"F1.opExtrude","SWEPT_FACE",FACE,{"disambiguationData":[OSD([sQuery(id+"F0.wireOp",EDGE,"E6.MirrorC")])]}),makeQuery(id+"F6.opExtrude","CAP_FACE",FACE,{"disambiguationData":[OSD([sQuery(id+"F5.wireOp",EDGE,"E45.0")])],"isStart":false})]});
            chamfer(context, id + "F7", {"entities" : qUnion([Q0, Q1]), "width" : 1 * mm, "tangentPropagation" : true});
        }
        {
            var Q0;
            Q0=makeQuery(id+"F1.opExtrude","CAP_FACE",FACE,{"disambiguationData":[OSD([sQuery(id+"F0.wireOp",EDGE,"E5"),sQuery(id+"F0.wireOp",EDGE,"E6.MirrorC"),sQuery(id+"F0.wireOp",EDGE,"E15.0"),sQuery(id+"F0.wireOp",EDGE,"E16.MirrorC"),sQuery(id+"F0.wireOp",EDGE,"E17"),sQuery(id+"F0.wireOp",EDGE,"E19.1.0"),sQuery(id+"F0.wireOp",EDGE,"E19.2.0"),sQuery(id+"F0.wireOp",EDGE,"E20"),sQuery(id+"F0.wireOp",EDGE,"E21.MirrorC"),sQuery(id+"F0.wireOp",EDGE,"E23.0"),sQuery(id+"F0.wireOp",EDGE,"E24.0"),sQuery(id+"F0.wireOp",EDGE,"E25.trimOffspring"),sQuery(id+"F0.wireOp",EDGE,"E26.trimOffspring"),sQuery(id+"F0.wireOp",EDGE,"E27.trimOffspring"),sQuery(id+"F0.wireOp",EDGE,"E28.trimOffspring"),sQuery(id+"F0.wireOp",EDGE,"E29.trimOffspring"),sQuery(id+"F0.wireOp",EDGE,"E31.trimOffspring"),sQuery(id+"F0.wireOp",EDGE,"E32.trimOffspring"),sQuery(id+"F0.wireOp",EDGE,"E34.trimOffspring"),sQuery(id+"F0.wireOp",EDGE,"E35.trimOffspring"),sQuery(id+"F0.wireOp",EDGE,"E39.trimOffspring"),sQuery(id+"F0.wireOp",EDGE,"E40.trimOffspring"),sQuery(id+"F0.wireOp",EDGE,"E41.trimOffspring"),sQuery(id+"F0.wireOp",EDGE,"E43.trimOffspring")])],"isStart":false});
            chamfer(context, id + "F8", {"entities" : qUnion([Q0]), "width" : .4 * mm, "tangentPropagation" : true});
        }
        {
            var Q0;
            Q0=makeQuery(id+"F1.opExtrude","CAP_FACE",FACE,{"disambiguationData":[OSD([sQuery(id+"F0.wireOp",EDGE,"E5"),sQuery(id+"F0.wireOp",EDGE,"E6.MirrorC"),sQuery(id+"F0.wireOp",EDGE,"E15.0"),sQuery(id+"F0.wireOp",EDGE,"E16.MirrorC"),sQuery(id+"F0.wireOp",EDGE,"E17"),sQuery(id+"F0.wireOp",EDGE,"E19.1.0"),sQuery(id+"F0.wireOp",EDGE,"E19.2.0"),sQuery(id+"F0.wireOp",EDGE,"E20"),sQuery(id+"F0.wireOp",EDGE,"E21.MirrorC"),sQuery(id+"F0.wireOp",EDGE,"E23.0"),sQuery(id+"F0.wireOp",EDGE,"E24.0"),sQuery(id+"F0.wireOp",EDGE,"E25.trimOffspring"),sQuery(id+"F0.wireOp",EDGE,"E26.trimOffspring"),sQuery(id+"F0.wireOp",EDGE,"E27.trimOffspring"),sQuery(id+"F0.wireOp",EDGE,"E28.trimOffspring"),sQuery(id+"F0.wireOp",EDGE,"E29.trimOffspring"),sQuery(id+"F0.wireOp",EDGE,"E31.trimOffspring"),sQuery(id+"F0.wireOp",EDGE,"E32.trimOffspring"),sQuery(id+"F0.wireOp",EDGE,"E34.trimOffspring"),sQuery(id+"F0.wireOp",EDGE,"E35.trimOffspring"),sQuery(id+"F0.wireOp",EDGE,"E39.trimOffspring"),sQuery(id+"F0.wireOp",EDGE,"E40.trimOffspring"),sQuery(id+"F0.wireOp",EDGE,"E41.trimOffspring"),sQuery(id+"F0.wireOp",EDGE,"E43.trimOffspring")])],"isStart":true});
            chamfer(context, id + "F9", {"entities" : qUnion([Q0]), "width" : 0.7 * mm, "tangentPropagation" : true});
        }
    });
